# Revit family: ISI_IdealStandard_BathScreens_Connect_T9923
name_source: partatom
category: Plumbing Fixtures
revit_build: Autodesk Revit MEP 2012 (Build: 20110309_2315(x64)
units: mm (PartAtom-declared; Revit-internal decimal feet)

## types (1)
- T9923EO - New Connect Angle Bath Screen
    Accessories = www.idealspec.co.uk
    AreaUnits = millimeters
    Assembly Code = C1030200
    AssetType = Fixed
    BIMObjectName = ISI_IdealStandard_ShowerEnclosures_Connect_T9923
    BREEAM = No
    BathType = Domestic
    Brand = Ideal Standard
    CWFU = 0
    CodePerformance = EN 14428:2004
    Color = Clear
    ConnectionType = PLUMBING
    Default Elevation = 1219 mm
    Description = New connect angle bath screen
    DrainSize = 0 mm  [stored 0 ft]
    DurationUnit = year
    ECA = No
    ExpectedLife = 30
    ExtrusionMaterial = ISI_IdealStandard_Baths_Chrome_Render
    Features = Angle bath screen
    Finish = Clear
    HWFU = 0
    HasGrabHandles = No
    IfcExportAs = IfcSanitaryTerminalType
    IfcExportType = BATH
    InstallationInstructions = www.idealspec.co.uk/resources.html
    LinearUnits = millimeters
    ManufacturerURL = www.idealspec.co.uk
    Material = Glass
    MaterialThickness = 5 mm  [stored 0.0164042 ft]
    Model = T9923EO
    ModelNumber = T9923EO
    ModelReference = New connect angle bath screen
    NBSDescription = Shower enclosures
    NBSReference = 45-35-70/332
    Name = ShowerEnclosures_Connect_T9923_IdealStandard
    NettWeight = 20 Kg
    NominalDepth = 40 mm
    NominalHeight = 1400 mm  [stored 4.59318 ft]
    NominalLength = 810 mm
    NominalWidth = 40 mm
    ProductInformation = www.idealspec.co.uk/datasheets/T9923EO
    ScreenMaterial = ISI_IdealStandard_Glass_Clear_Render
    Shape = Rectangular
    Size = 1400 x 810 x 40 mm
    Space = Internal
    SpareParts = www.fastpart-spares.co.uk
    TMV3 = No
    URL = www.idealspec.co.uk
    Uniclass2 = Pr_40_20_06_79
    Version = 2
    VolumeUnits = Litres
    WFU = 0
    WRAS = No
    WarrantyDescription = Manufacturers warranty
    WarrantyDurationParts = 10
    WarrantyDurationUnit = year
    WaterEfficientProduct = No

note: [stored X ft] marks values corroborated as IEEE doubles in the binary element streams (Revit-internal decimal feet)

## geometry (parser evidence)
native form markers: Blend x2, Extrusion x1, Sweep x2
no freeform markers — native parametric forms only
